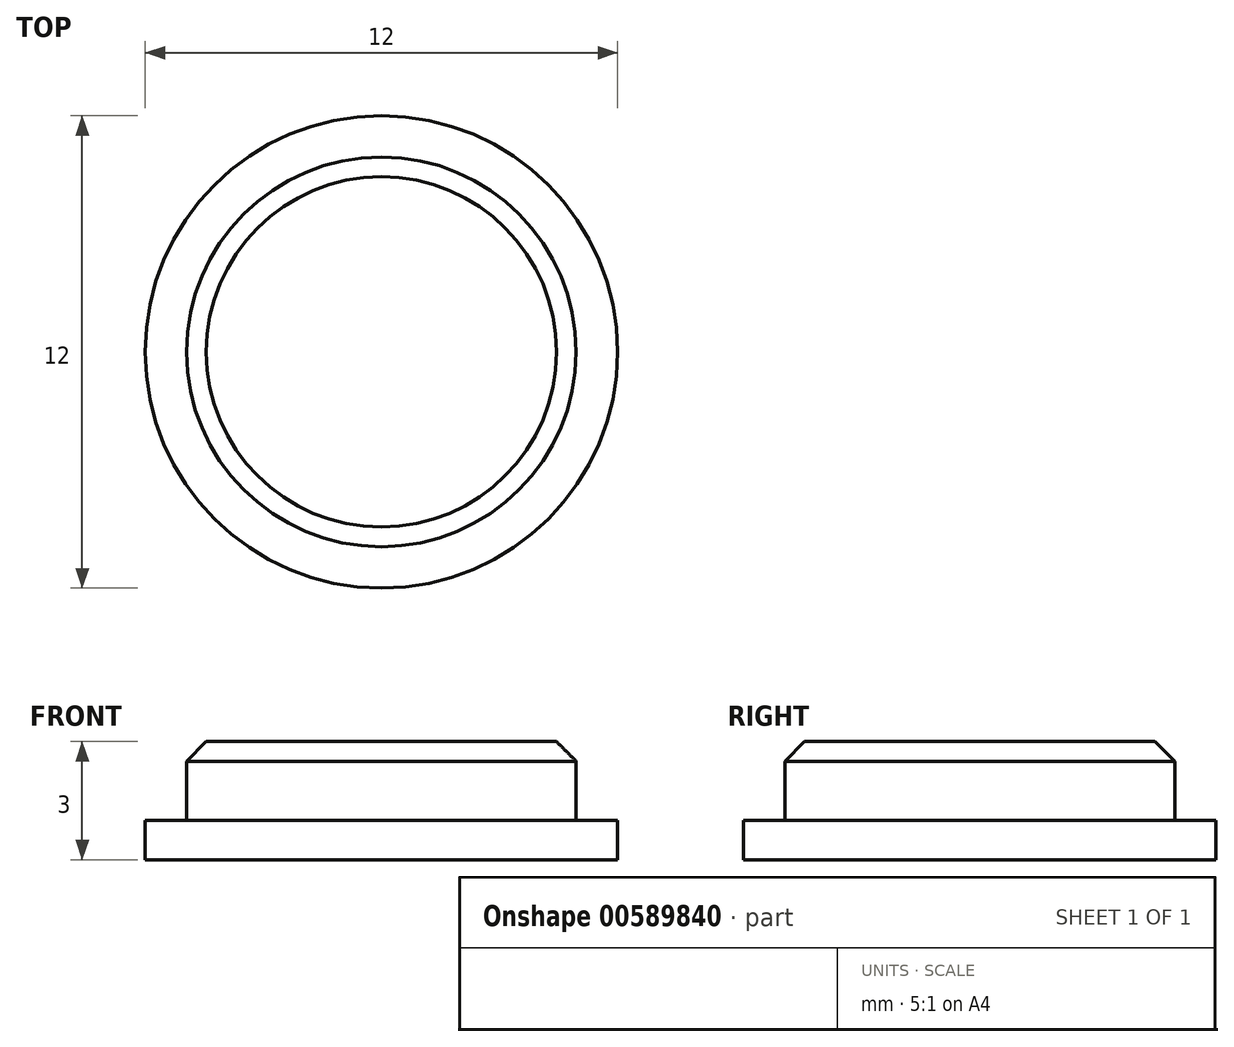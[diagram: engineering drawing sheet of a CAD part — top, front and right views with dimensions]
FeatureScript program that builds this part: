
annotation { "Feature Type Name" : "Feature", "Feature Type Description" : "" }
export const myFeature = defineFeature(function(context is Context, id is Id, definition is map)
    precondition{}
    {
        {
            var Q0;
            Q0=qCreatedBy(makeId("Top.planeOp"),FACE);
            var sketch = newSketch(context, id + "F0", { "sketchPlane" : qUnion([Q0])});
            skCircle(sketch, "E0", {"center": v(-42.84, 43.44) * mm, "radius": 6 * mm});
            skCircle(sketch, "E1", {"center": v(-42.84, 43.44) * mm, "radius": 4.95 * mm});
            skSolve(sketch);
        }
        {
            var Q0;
            Q0=makeQuery(id+"F0.imprint","IMPRINT",FACE,{"disambiguationData":[TD([[makeQuery(id+"F0.imprint","IMPRINT",EDGE,{"derivedFrom":sQuery(id+"F0.wireOp",EDGE,"E1")}),1.0]])]});
            extrude(context, id + "F1", {"entities" : qUnion([Q0]), "depth" : 3 * mm, "offsetDistance" : 25 * mm});
        }
        {
            var Q0;
            Q0=makeQuery(id+"F1.opExtrude","CAP_FACE",FACE,{"disambiguationData":[OSD([sQuery(id+"F0.wireOp",EDGE,"E1")])],"isStart":true});
            var sketch = newSketch(context, id + "F2", { "sketchPlane" : qUnion([Q0])});
            skCircle(sketch, "E2", {"center": v(-42.84, -43.44) * mm, "radius": 6 * mm});
            skSolve(sketch);
        }
        {
            var Q0;
            Q0=makeQuery(id+"F2.imprint","IMPRINT",FACE,{"disambiguationData":[TD([[makeQuery(id+"F2.imprint","IMPRINT",EDGE,{"derivedFrom":sQuery(id+"F2.wireOp",EDGE,"E2")}),1.0]])]});
            extrude(context, id + "F3", {"entities" : qUnion([Q0]), "operationType" : NewBodyOperationType.ADD, "oppositeDirection" : true, "depth" : 1 * mm, "offsetDistance" : 25 * mm});
        }
        {
            var Q0;
            Q0=makeQuery(id+"F1.opExtrude","CAP_EDGE",EDGE,{"disambiguationData":[OSD([sQuery(id+"F0.wireOp",EDGE,"E1")])],"isStart":false});
            chamfer(context, id + "F4", {"entities" : qUnion([Q0]), "width" : 0.5 * mm, "tangentPropagation" : true});
        }
    });
